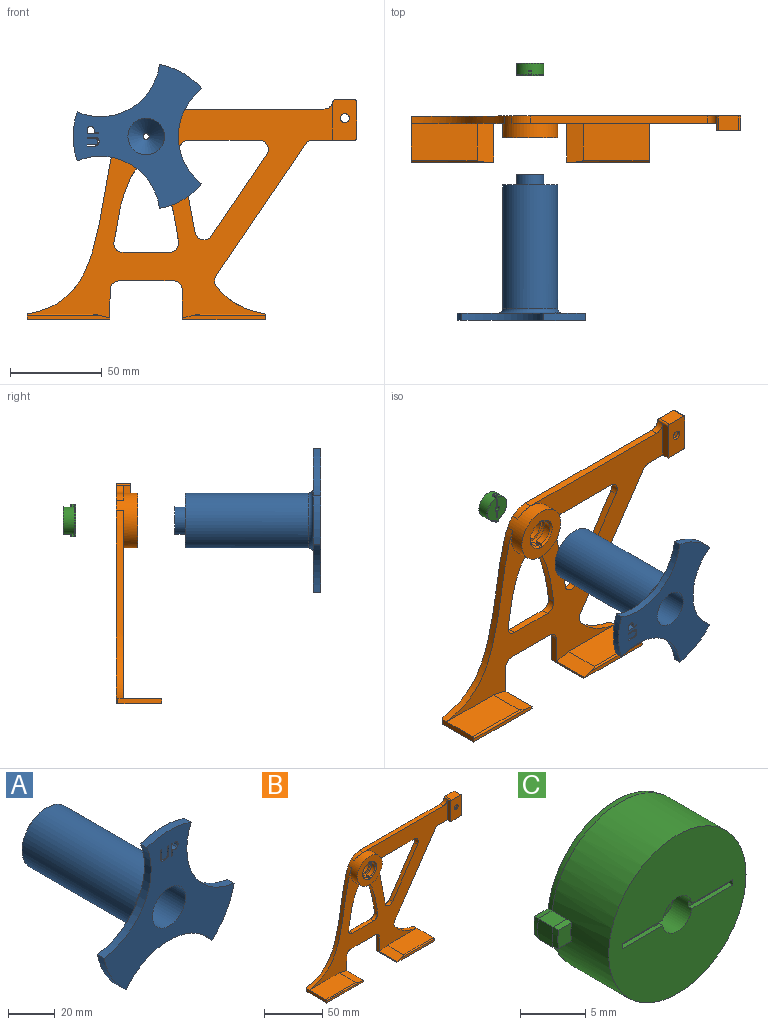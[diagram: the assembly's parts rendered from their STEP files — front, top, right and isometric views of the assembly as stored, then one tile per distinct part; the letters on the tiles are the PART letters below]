
ASSEMBLY  parts=3 mates=2
PART A: 38 faces, bbox 78.7x79.5x70.4 mm
  f0: cylinder r=10mm len=60mm, axis (0,1,0), area 3769.9mm2, adj f29,f33
  f1: plane 4.18x4mm, normal (1,0,0), area 16.7mm2, adj f2,f26,f29,f30
  f2: plane 4x0.75mm, normal (0,0,-1), area 3mm2, adj f1,f3,f29,f30
  f3: plane 4.15x4mm, normal (-1,0,0), area 16.6mm2, adj f2,f4,f29,f30
  f4: extruded ~4x1.73mm, area 7.6mm2, adj f3,f5,f29,f30
  f5: extruded ~4x1.82mm, area 7.9mm2, adj f4,f6,f29,f30
  f6: extruded ~4x1.79mm, area 7.8mm2, adj f5,f7,f29,f30
  f7: extruded ~4x1.74mm, area 7.6mm2, adj f6,f8,f29,f30
  f8: plane 4.14x4mm, normal (1,0,0), area 16.6mm2, adj f7,f9,f29,f30
  f9: plane 4x0.75mm, normal (0,0,-1), area 3mm2, adj f8,f10,f29,f30
  f10: plane 4.19x4mm, normal (-1,0,0), area 16.8mm2, adj f9,f11,f29,f30
  f11: extruded ~4x1.23mm, area 5.4mm2, adj f10,f12,f29,f30
  f12: extruded ~4x1.29mm, area 5.6mm2, adj f11,f13,f29,f30
  f13: extruded ~4x1.25mm, area 5.4mm2, adj f12,f26,f29,f30
  f14: plane 4x1.67mm, normal (0,0,-1), area 6.7mm2, adj f15,f27,f29,f30
  f15: extruded ~4x2.41mm, area 13.9mm2, adj f14,f16,f29,f30
  f16: extruded ~4x1.5mm, area 6.8mm2, adj f15,f17,f29,f30
  f17: extruded ~4x1.9mm, area 8mm2, adj f16,f18,f29,f30
  f18: plane 4x0.76mm, normal (0,0,1), area 3mm2, adj f17,f19,f29,f30
  f19: plane 4x2.53mm, normal (-1,0,0), area 10.1mm2, adj f18,f20,f29,f30
  f20: plane 4x0.75mm, normal (0,0,1), area 3mm2, adj f19,f27,f29,f30
  f21: cylinder r=32.5mm len=51.91mm, axis (0,1,0), area 240.5mm2, adj f22,f28,f29,f30
  f22: cylinder r=40mm len=23.18mm, axis (0,1,0), area 109.2mm2, adj f21,f23,f29,f30
  f23: cylinder r=32.5mm len=44.95mm, axis (0,1,0), area 240.5mm2, adj f22,f24,f29,f30
  f24: cylinder r=40mm len=26.77mm, axis (0,1,0), area 109.2mm2, adj f23,f25,f29,f30
  f25: cylinder r=32.5mm len=44.95mm, axis (0,1,0), area 240.5mm2, adj f24,f28,f29,f30
  f26: extruded ~4x1.24mm, area 5.4mm2, adj f1,f13,f29,f30
  f27: plane 6.42x4mm, normal (1,0,0), area 25.7mm2, adj f14,f20,f29,f30
  f28: cylinder r=40mm len=23.18mm, axis (0,1,0), area 109.2mm2, adj f21,f25,f29,f30
  f29: plane 78.67x70.44mm, normal (0,-1,0), area 2258.7mm2, adj f0,f1,f2,f3,f4,f5,f6,f7
  f30: plane 78.67x70.44mm, normal (0,1,0), area 1621.7mm2, adj f1,f2,f3,f4,f5,f6,f7,f8
  f31: plane 30x30mm, normal (0,1,0), area 532.5mm2, adj f32,f35
  f32: cylinder r=15mm len=67.6mm, axis (0,1,0), area 6371.1mm2, adj f31,f34
  f33: cone r=1mm half-angle=45deg, axis (0,-1,0), area 432.9mm2, adj f0,f37
  f34: torus R=17.4mm, axis (0,-1,0), area 376mm2, adj f30,f32
  f35: cylinder r=7.45mm len=14.9mm, axis (0,-1,0), area 257.5mm2, adj f31,f36
  f36: plane 14.9x14.9mm, normal (0,1,0), area 166.3mm2, adj f35,f37
  f37: cylinder r=1.6mm len=11.1mm, axis (0,-1,0), area 111.6mm2, adj f33,f36
PART B: 77 faces, bbox 180x25x120 mm
  f0: cylinder r=2.5mm len=5mm, axis (0,1,0), area 23.6mm2, adj f27,f75
  f1: plane 18x18mm, normal (0,-1,0), area 77.8mm2, adj f25,f34
  f2: plane 167.01x119.17mm, normal (0,-1,0), area 6042.7mm2, adj f3,f6,f7,f8,f9,f10,f13,f14
  f3: extruded ~102.6x51.09mm, area 491.4mm2, adj f2,f11,f26,f35,f49
  f4: extruded ~10.06x4mm, area 44.3mm2, adj f5,f10,f26,f35
  f5: plane 10.27x4.09mm, normal (0,-1,0), area 0.7mm2, adj f4,f35
  f6: plane 44.45x30.15mm, normal (-0.83,0,0.56), area 214.8mm2, adj f2,f26,f56,f58
  f7: extruded ~44.41x8.26mm, area 180.7mm2, adj f2,f26,f56,f57
  f8: plane 25.31x4mm, normal (0,0,1), area 101.2mm2, adj f2,f26,f52,f53
  f9: plane 21x4mm, normal (-1,0,0), area 84mm2, adj f2,f20,f27,f47
  f10: plane 97.08x4mm, normal (0,0,1), area 388.3mm2, adj f2,f4,f26,f50
  f11: plane 24x3mm, normal (-1,0,0), area 71.8mm2, adj f3,f12,f29,f30,f49,f65
  f12: plane 45x25mm, normal (0,0,-1), area 1124.8mm2, adj f11,f13,f26,f28,f30,f49
  f13: extruded ~16.31x4mm, area 65.3mm2, adj f2,f12,f26,f51
  f14: plane 29.38x4mm, normal (0,0,-1), area 117.5mm2, adj f2,f26,f51,f54
  f15: extruded ~16.31x4mm, area 65.3mm2, adj f2,f16,f26,f54
  f16: plane 45x25mm, normal (0,0,-1), area 1124.8mm2, adj f15,f17,f26,f32,f33,f48
  f17: plane 24x3mm, normal (1,0,0), area 71.8mm2, adj f16,f18,f31,f33,f48,f64
  f18: extruded ~26.67x15.11mm, area 125.5mm2, adj f2,f17,f26,f48,f55
  f19: plane 71.87x48.75mm, normal (0.83,0,-0.56), area 347.4mm2, adj f2,f26,f55,f59
  f20: plane 22.94x8mm, normal (0,0,-1), area 139.8mm2, adj f2,f9,f26,f27,f45,f59
  f21: plane 20x8mm, normal (1,0,0), area 160mm2, adj f26,f27,f45,f46
  f22: plane 38.42x4mm, normal (0,0,-1), area 153.7mm2, adj f2,f26,f57,f58
  f23: extruded ~42.73x35.23mm, area 387.3mm2, adj f2,f26,f52,f53
  f24: plane 11x8mm, normal (0,0,1), area 88mm2, adj f26,f27,f46,f47
  f25: cylinder r=7.5mm len=15mm, axis (0,1,0), area 188.5mm2, adj f1,f26
  f26: plane 180x120mm, normal (0,1,0), area 7041.1mm2, adj f3,f4,f6,f7,f8,f10,f12,f13
  f27: plane 22x13mm, normal (0,-1,0), area 265.7mm2, adj f0,f9,f20,f21,f24,f45,f46,f47
  f28: plane 21x1mm, normal (1,0,0), area 21mm2, adj f2,f12,f30,f60
  f29: plane 36x20mm, normal (0,0,1), area 720mm2, adj f2,f11,f60,f65
  f30: plane 45x2mm, normal (0,-1,0), area 87.7mm2, adj f11,f12,f28,f60,f65
  f31: plane 36x20mm, normal (0,0,1), area 720mm2, adj f2,f17,f61,f64
  f32: plane 21x1mm, normal (-1,0,0), area 21mm2, adj f2,f16,f33,f61
  f33: plane 45x2mm, normal (0,-1,0), area 87.7mm2, adj f16,f17,f32,f61,f64
  f34: cylinder r=9mm len=18mm, axis (0,1,0), area 189.7mm2, adj f1,f36,f37,f38,f40,f41,f43,f44
  f35: cylinder r=15mm len=30mm, axis (0,1,0), area 781.2mm2, adj f2,f3,f4,f5,f26,f43
  f36: plane 17.89x8mm, normal (0,1,0), area 35.9mm2, adj f34,f37,f41,f42
  f37: plane 5.01x1.52mm, normal (1,0,0), area 7.1mm2, adj f34,f36,f42,f43,f62
  f38: plane 5.01x1.52mm, normal (-1,0,0), area 7.1mm2, adj f34,f39,f43,f44,f63
  f39: cylinder r=7.5mm len=14.87mm, axis (0,1,0), area 86.2mm2, adj f38,f40,f44,f63
  f40: plane 5.01x1.52mm, normal (-1,0,0), area 7.1mm2, adj f34,f39,f43,f44,f63
  f41: plane 5.01x1.52mm, normal (1,0,0), area 7.1mm2, adj f34,f36,f42,f43,f62
  f42: cylinder r=7.5mm len=14.87mm, axis (0,1,0), area 86.2mm2, adj f36,f37,f41,f62
  f43: plane 30x30mm, normal (0,-1,0), area 477.9mm2, adj f34,f35,f37,f38,f40,f41,f62,f63
  f44: plane 17.89x8mm, normal (0,1,0), area 35.9mm2, adj f34,f38,f39,f40
  f45: cylinder r=1mm len=8mm, axis (0,1,0), area 12.6mm2, adj f20,f21,f26,f27
  f46: cylinder r=1mm len=8mm, axis (0,1,0), area 12.6mm2, adj f21,f24,f26,f27
  f47: cylinder r=1mm len=8mm, axis (0,1,0), area 11.9mm2, adj f2,f9,f24,f26,f27,f50
  f48: cylinder r=1mm len=3.18mm, axis (0,0,1), area 4.8mm2, adj f16,f17,f18,f26
  f49: cylinder r=1mm len=3.18mm, axis (0,0,-1), area 4.8mm2, adj f3,f11,f12,f26
  f50: cylinder r=5mm len=4.93mm, axis (0,1,0), area 28.1mm2, adj f2,f10,f26,f47
  f51: cylinder r=5mm len=5mm, axis (0,1,0), area 30.6mm2, adj f2,f13,f14,f26
  f52: cylinder r=5mm len=5.63mm, axis (0,1,0), area 34mm2, adj f2,f8,f23,f26
  f53: cylinder r=5mm len=5.63mm, axis (0,1,0), area 34mm2, adj f2,f8,f23,f26
  f54: cylinder r=5mm len=5mm, axis (0,1,0), area 30.6mm2, adj f2,f14,f15,f26
  f55: cylinder r=5mm len=5.82mm, axis (0,1,0), area 24.9mm2, adj f2,f18,f19,f26
  f56: cylinder r=5mm len=9.02mm, axis (0,1,0), area 46.5mm2, adj f2,f6,f7,f26
  f57: cylinder r=5mm len=6.13mm, axis (0,1,0), area 36mm2, adj f2,f7,f22,f26
  f58: cylinder r=5mm len=7.81mm, axis (0,-1,0), area 43.3mm2, adj f2,f6,f22,f26
  f59: cylinder r=5mm len=4.14mm, axis (0,1,0), area 19.5mm2, adj f2,f19,f20,f26
  f60: plane 21x9mm, normal (0.22,0,0.98), area 192.6mm2, adj f2,f28,f29,f30,f65
  f61: plane 21x9mm, normal (-0.22,0,0.98), area 192.6mm2, adj f2,f31,f32,f33,f64
  f62: cone r=7.5mm half-angle=45deg, axis (0,-1,0), area 32.7mm2, adj f37,f41,f42,f43
  f63: cone r=7.5mm half-angle=45deg, axis (0,-1,0), area 32.7mm2, adj f38,f39,f40,f43
  f64: cylinder r=1mm len=40.5mm, axis (1,0,0), area 59.1mm2, adj f17,f31,f33,f61
  f65: cylinder r=1mm len=40.5mm, axis (1,0,0), area 59.1mm2, adj f11,f29,f30,f60
  f66: cylinder r=2.5mm len=5mm, axis (0,1,0), area 15.7mm2, adj f67,f76
  f67: plane 9x9mm, normal (0,1,0), area 44mm2, adj f66,f68
  f68: cylinder r=4.5mm len=9mm, axis (0,1,0), area 56.5mm2, adj f26,f67
  f69: plane 4.21x3.5mm, normal (0,0,-1), area 14.8mm2, adj f70,f74,f75,f76
  f70: plane 3.65x3.5mm, normal (-0.87,0,-0.5), area 14.8mm2, adj f69,f71,f75,f76
  f71: plane 3.65x3.5mm, normal (-0.87,0,0.5), area 14.8mm2, adj f70,f72,f75,f76
  f72: plane 4.21x3.5mm, normal (0,0,1), area 14.8mm2, adj f71,f73,f75,f76
  f73: plane 3.65x3.5mm, normal (0.87,0,0.5), area 14.8mm2, adj f72,f74,f75,f76
  f74: plane 3.65x3.5mm, normal (0.87,0,-0.5), area 14.8mm2, adj f69,f73,f75,f76
  f75: plane 8.43x7.3mm, normal (0,1,0), area 26.5mm2, adj f0,f69,f70,f71,f72,f73,f74
  f76: plane 8.43x7.3mm, normal (0,-1,0), area 26.5mm2, adj f66,f69,f70,f71,f72,f73,f74
PART C: 51 faces, bbox 17.9x6.7x14.9 mm
  f0: plane 17.72x14.72mm, normal (0,1,0), area 163mm2, adj f11,f12,f13,f14,f15,f16,f17,f18
  f1: plane 1.72x1.46mm, normal (0,-1,0), area 2.4mm2, adj f8,f19,f20,f21
  f2: plane 1.6x1.51mm, normal (0,0,-1), area 2.4mm2, adj f3,f8,f12,f24
  f3: cylinder r=8.95mm len=1.9mm, axis (0,1,0), area 3mm2, adj f2,f4,f14,f23
  f4: plane 1.6x1.51mm, normal (0,0,1), area 2.4mm2, adj f3,f8,f16,f22
  f5: plane 1.6x1.51mm, normal (0,0,1), area 2.4mm2, adj f6,f8,f17,f19
  f6: cylinder r=8.95mm len=1.9mm, axis (0,1,0), area 3mm2, adj f5,f7,f15,f20
  f7: plane 1.6x1.51mm, normal (0,0,-1), area 2.4mm2, adj f6,f8,f13,f21
  f8: cylinder r=7.45mm len=14.9mm, axis (0,1,0), area 282.3mm2, adj f1,f2,f4,f5,f7,f9,f10,f11
  f9: plane 1.72x1.46mm, normal (0,-1,0), area 2.4mm2, adj f8,f22,f23,f24
  f10: plane 14.9x14.9mm, normal (0,-1,0), area 161.9mm2, adj f8,f25,f44,f45,f46,f47,f48,f50
  f11: cone r=7.45mm half-angle=10deg, axis (0,-1,0), area 10.9mm2, adj f0,f8,f12,f13
  f12: plane 1.59x0.5mm, normal (0,0.17,-0.98), area 0.8mm2, adj f0,f2,f11,f14
  f13: plane 1.59x0.5mm, normal (0,0.17,-0.98), area 0.8mm2, adj f0,f7,f11,f15
  f14: cone r=8.95mm half-angle=10deg, axis (0,-1,0), area 0.9mm2, adj f0,f3,f12,f16
  f15: cone r=8.86mm half-angle=10deg, axis (0,-1,0), area 0.9mm2, adj f0,f6,f13,f17
  f16: plane 1.59x0.5mm, normal (0,0.17,0.98), area 0.8mm2, adj f0,f4,f14,f18
  f17: plane 1.59x0.5mm, normal (0,0.17,0.98), area 0.8mm2, adj f0,f5,f15,f18
  f18: cone r=7.45mm half-angle=10deg, axis (0,-1,0), area 10.9mm2, adj f0,f8,f16,f17
  f19: plane 1.51x0.5mm, normal (0,-0.17,0.98), area 0.7mm2, adj f1,f5,f8,f20
  f20: cone r=8.95mm half-angle=10deg, axis (0,1,0), area 0.9mm2, adj f1,f6,f19,f21
  f21: plane 1.51x0.5mm, normal (0,-0.17,-0.98), area 0.7mm2, adj f1,f7,f8,f20
  f22: plane 1.51x0.5mm, normal (0,-0.17,0.98), area 0.7mm2, adj f4,f8,f9,f23
  f23: cone r=8.86mm half-angle=10deg, axis (0,1,0), area 0.9mm2, adj f3,f9,f22,f24
  f24: plane 1.51x0.5mm, normal (0,-0.17,-0.98), area 0.7mm2, adj f2,f8,f9,f23
  f25: cylinder r=1.6mm len=3.2mm, axis (0,-1,0), area 19.7mm2, adj f10,f34,f43,f44,f45,f47,f48,f49
  f26: cylinder r=1.6mm len=3.2mm, axis (0,-1,0), area 18.7mm2, adj f0,f33,f35,f36,f37,f39,f40,f41
  f27: plane 2.85x2.8mm, normal (0.87,0,-0.5), area 9.2mm2, adj f28,f32,f33,f34
  f28: plane 2.85x2.8mm, normal (0.87,0,0.5), area 9.2mm2, adj f27,f29,f33,f34
  f29: plane 3.29x2.8mm, normal (0,0,1), area 9.2mm2, adj f28,f30,f33,f34
  f30: plane 2.85x2.8mm, normal (-0.87,0,0.5), area 9.2mm2, adj f29,f31,f33,f34
  f31: plane 2.85x2.8mm, normal (-0.87,0,-0.5), area 9.2mm2, adj f30,f32,f33,f34
  f32: plane 3.29x2.8mm, normal (0,0,-1), area 9.2mm2, adj f27,f31,f33,f34
  f33: plane 6.58x5.7mm, normal (0,-1,0), area 20.1mm2, adj f26,f27,f28,f29,f30,f31,f32
  f34: plane 6.58x5.7mm, normal (0,1,0), area 20.1mm2, adj f25,f27,f28,f29,f30,f31,f32
  f35: plane 4.42x0.5mm, normal (0,1,0), area 2.2mm2, adj f26,f36,f37,f38
  f36: plane 4.42x0.4mm, normal (0,0,-1), area 1.8mm2, adj f0,f26,f35,f38
  f37: plane 4.42x0.4mm, normal (0,0,1), area 1.8mm2, adj f0,f26,f35,f38
  f38: plane 0.5x0.4mm, normal (-1,0,0), area 0.2mm2, adj f0,f35,f36,f37
  f39: plane 4.42x0.4mm, normal (0,0,1), area 1.8mm2, adj f0,f26,f41,f42
  f40: plane 4.42x0.4mm, normal (0,0,-1), area 1.8mm2, adj f0,f26,f41,f42
  f41: plane 4.42x0.5mm, normal (0,1,0), area 2.2mm2, adj f26,f39,f40,f42
  f42: plane 0.5x0.4mm, normal (1,0,0), area 0.2mm2, adj f0,f39,f40,f41
  f43: plane 4.42x0.5mm, normal (0,-1,0), area 2.2mm2, adj f25,f44,f45,f46
  f44: plane 4.42x0.4mm, normal (0,0,-1), area 1.8mm2, adj f10,f25,f43,f46
  f45: plane 4.42x0.4mm, normal (0,0,1), area 1.8mm2, adj f10,f25,f43,f46
  f46: plane 0.5x0.4mm, normal (-1,0,0), area 0.2mm2, adj f10,f43,f44,f45
  f47: plane 4.42x0.4mm, normal (0,0,1), area 1.8mm2, adj f10,f25,f49,f50
  f48: plane 4.42x0.4mm, normal (0,0,-1), area 1.8mm2, adj f10,f25,f49,f50
  f49: plane 4.42x0.5mm, normal (0,-1,0), area 2.2mm2, adj f25,f47,f48,f50
  f50: plane 0.5x0.4mm, normal (1,0,0), area 0.2mm2, adj f10,f47,f48,f49
PLACE A rot(axis=(0,-1,0),90deg) t=(-30.55,-38.43,1.4)mm
PLACE B t=(-30.55,-7.44,1.4)mm fixed
PLACE C rot(axis=(-0.71,0,0.71),180deg) t=(-30.55,46.56,1.4)mm
MATE cylindrical C.f3 <-> B.f25  axis (0,-1,0) through (-30.55,14.56,1.4)mm
MATE slider C.f3 <-> A.f0  axis (0,-1,0) through (-30.55,14.56,1.4)mm
